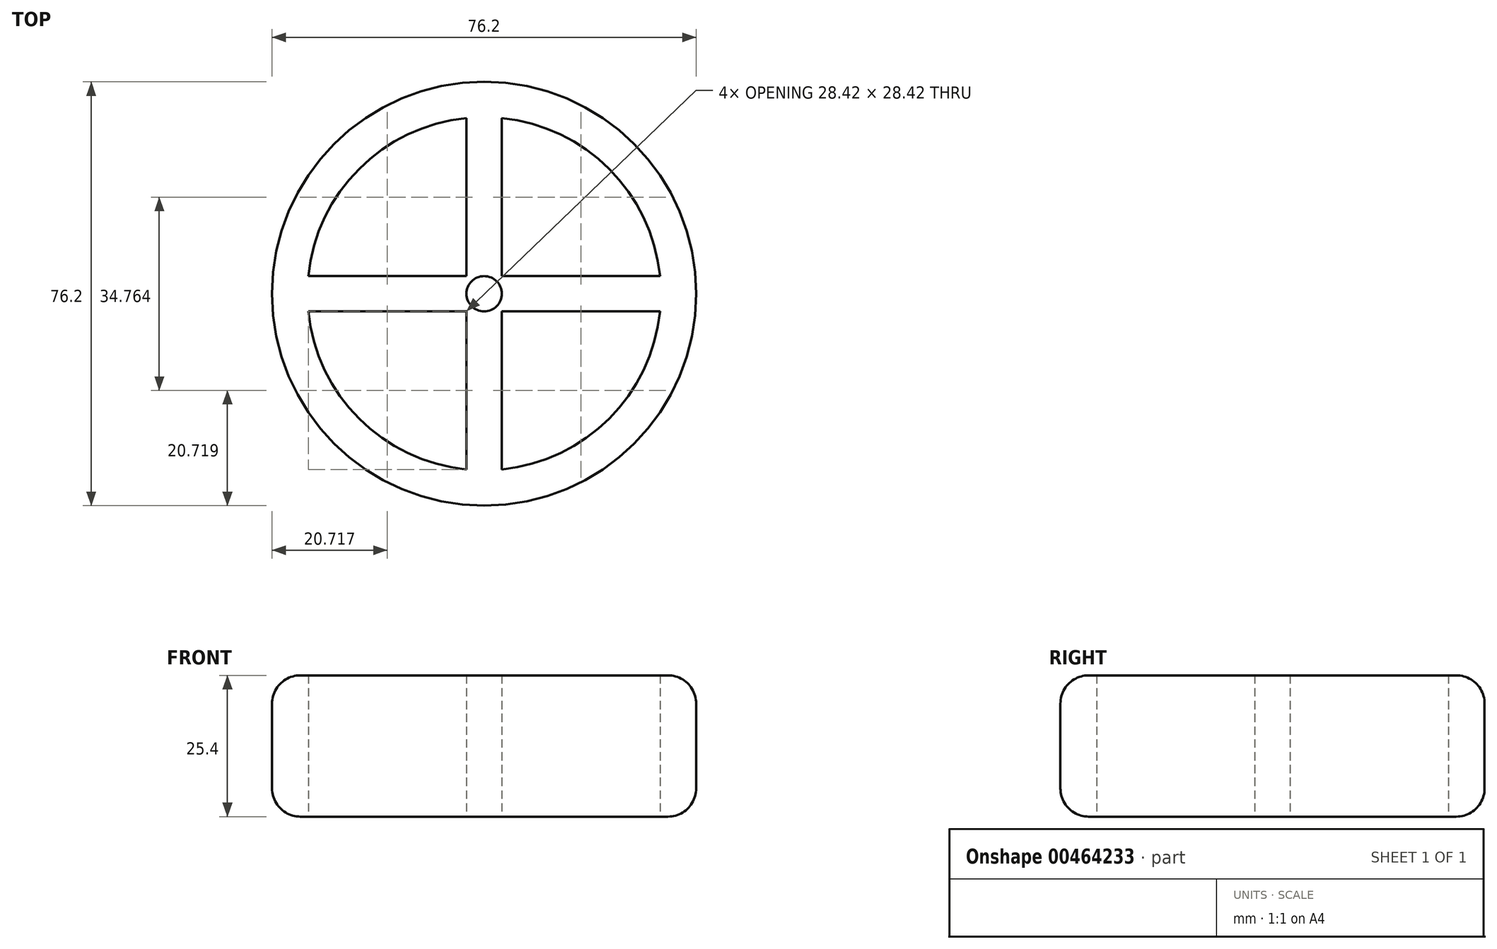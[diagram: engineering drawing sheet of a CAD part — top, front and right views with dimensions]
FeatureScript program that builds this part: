
annotation { "Feature Type Name" : "Feature", "Feature Type Description" : "" }
export const myFeature = defineFeature(function(context is Context, id is Id, definition is map)
    precondition{}
    {
        {
            var Q0;
            Q0=qCreatedBy(makeId("Top.planeOp"),FACE);
            var sketch = newSketch(context, id + "F0", { "sketchPlane" : qUnion([Q0])});
            skCircle(sketch, "E0", {"center": v(0, 0) * mm, "radius": 38.1 * mm});
            skArc(sketch, "E1", {"start": v(-31.6, -3.17) * mm, "mid": v(-22.45, -22.45) * mm, "end": v(-3.18, -31.6) * mm});
            skCircle(sketch, "E2", {"center": v(0, 0) * mm, "radius": 0.64 * mm});
            skCircle(sketch, "E3", {"center": v(0, 0) * mm, "radius": 3.18 * mm});
            skLineSegment(sketch, "E4", {"start": v(0, 0) * mm, "end": v(0, 3.18) * mm});
            skLineSegment(sketch, "E5", {"start": v(0, 0) * mm, "end": v(3.18, 0) * mm});
            skLineSegment(sketch, "E6", {"start": v(0, 0) * mm, "end": v(0, -3.18) * mm});
            skLineSegment(sketch, "E7", {"start": v(0, 0) * mm, "end": v(-3.18, 0) * mm});
            skLineSegment(sketch, "E8", {"start": v(3.18, 3.18) * mm, "end": v(3.18, 31.6) * mm});
            skLineSegment(sketch, "E9", {"start": v(-3.18, 3.18) * mm, "end": v(-3.18, 31.6) * mm});
            skLineSegment(sketch, "E10", {"start": v(3.18, -3.17) * mm, "end": v(31.6, -3.17) * mm});
            skLineSegment(sketch, "E11", {"start": v(3.18, 3.18) * mm, "end": v(31.6, 3.18) * mm});
            skLineSegment(sketch, "E12", {"start": v(3.18, -3.17) * mm, "end": v(3.18, -31.6) * mm});
            skLineSegment(sketch, "E13", {"start": v(-3.18, -3.17) * mm, "end": v(-3.18, -31.6) * mm});
            skLineSegment(sketch, "E14", {"start": v(-3.18, 3.18) * mm, "end": v(-31.6, 3.18) * mm});
            skLineSegment(sketch, "E15", {"start": v(0.16, -3.17) * mm, "end": v(-0.16, -3.17) * mm});
            skArc(sketch, "E16.trimOffspring", {"start": v(31.6, 3.17) * mm, "mid": v(22.45, 22.45) * mm, "end": v(3.18, 31.6) * mm});
            skArc(sketch, "E17.trimOffspring", {"start": v(3.17, -31.6) * mm, "mid": v(22.45, -22.45) * mm, "end": v(31.6, -3.17) * mm});
            skArc(sketch, "E18.trimOffspring", {"start": v(-3.18, 31.6) * mm, "mid": v(-22.45, 22.45) * mm, "end": v(-31.6, 3.18) * mm});
            skPoint(sketch, "E19.orphan", {"position": v(0, 3.18) * mm});
            skLineSegment(sketch, "E20.trimOffspring", {"start": v(-3.18, -3.17) * mm, "end": v(-31.6, -3.17) * mm});
            skSolve(sketch);
        }
        {
            var Q0;
            Q0 = qSketchRegion(id + "F0", true);
            extrude(context, id + "F1", {"entities" : qUnion([Q0]), "depth" : 25.4 * mm});
        }
        {
            var Q0;
            Q0=makeQuery(id+"F1.opExtrude","CAP_EDGE",EDGE,{"disambiguationData":[OSD([sQuery(id+"F0.wireOp",EDGE,"E0")])],"isStart":true});
            var Q1;
            Q1=makeQuery(id+"F1.opExtrude","SWEPT_FACE",FACE,{"disambiguationData":[OSD([sQuery(id+"F0.wireOp",EDGE,"E0")])]});
            fillet(context, id + "F2", {"entities" : qUnion([Q0, Q1]), "radius" : 5.08 * mm, "tangentPropagation" : true, "allowEdgeOverflow" : false});
        }
    });
